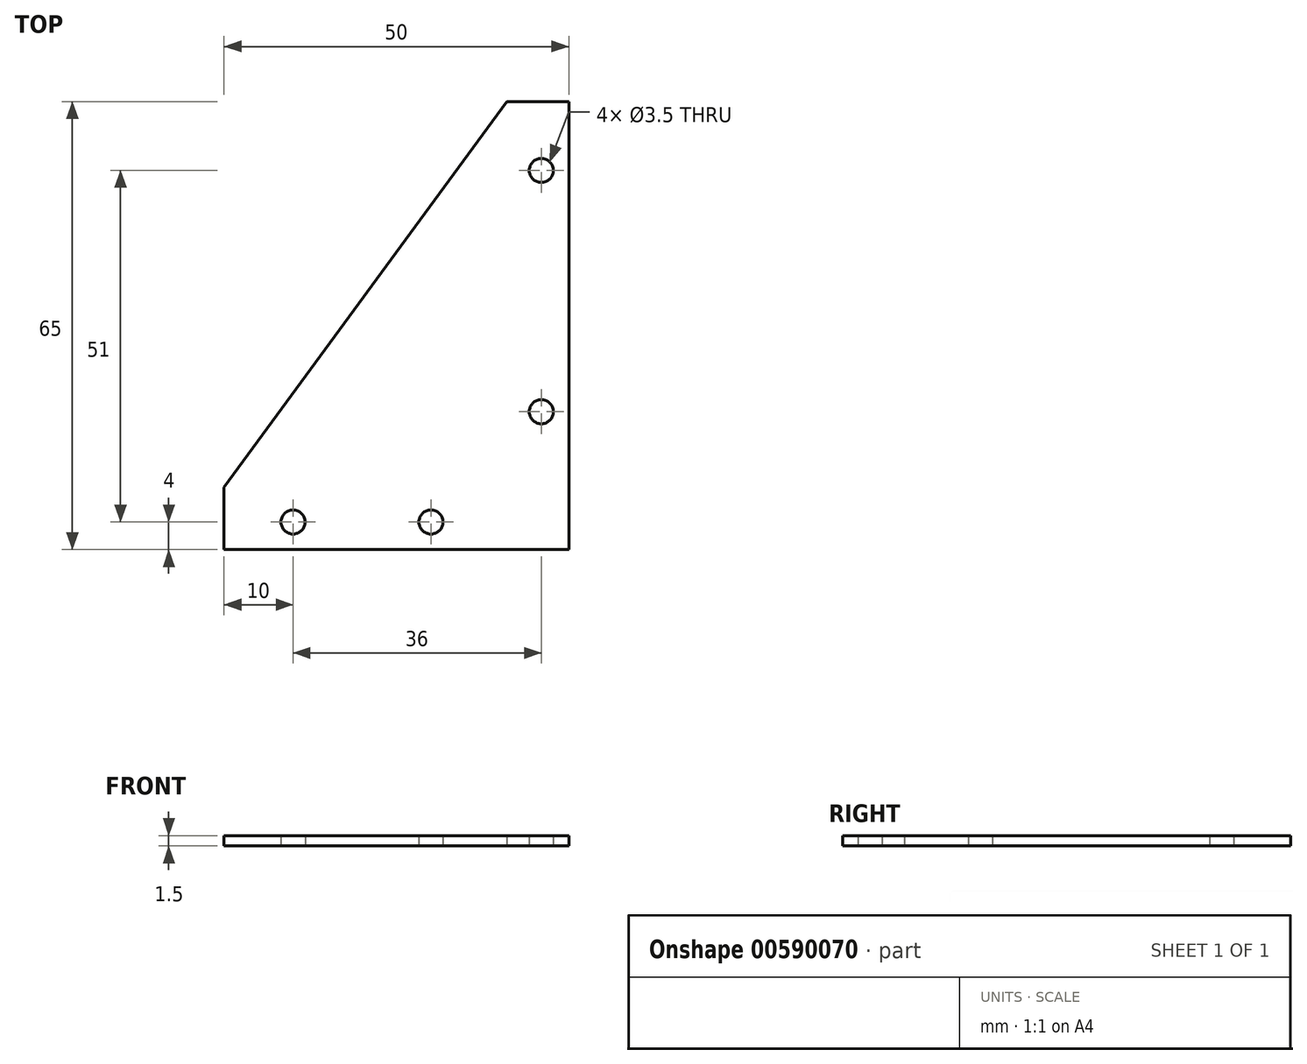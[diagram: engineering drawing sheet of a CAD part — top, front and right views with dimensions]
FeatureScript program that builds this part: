
annotation { "Feature Type Name" : "Feature", "Feature Type Description" : "" }
export const myFeature = defineFeature(function(context is Context, id is Id, definition is map)
    precondition{}
    {
        {
            var Q0;
            Q0=qCreatedBy(makeId("Top.planeOp"),FACE);
            var sketch = newSketch(context, id + "F0", { "sketchPlane" : qUnion([Q0])});
            skLineSegment(sketch, "E0.bottom", {"start": v(0, 0) * mm, "end": v(-50, 0) * mm});
            skLineSegment(sketch, "E0.top", {"start": v(0, 65) * mm, "end": v(-50, 65) * mm});
            skLineSegment(sketch, "E0.left", {"start": v(0, 0) * mm, "end": v(0, 65) * mm});
            skLineSegment(sketch, "E0.right", {"start": v(-50, 0) * mm, "end": v(-50, 65) * mm});
            skLineSegment(sketch, "E1", {"start": v(-9, 65) * mm, "end": v(-50, 9) * mm});
            skCircle(sketch, "E2", {"center": v(-4, 55) * mm, "radius": 1.75 * mm});
            skCircle(sketch, "E3", {"center": v(-40, 4) * mm, "radius": 1.75 * mm});
            skCircle(sketch, "E4", {"center": v(-20, 4) * mm, "radius": 1.75 * mm});
            skCircle(sketch, "E5", {"center": v(-4, 20) * mm, "radius": 1.75 * mm});
            skSolve(sketch);
        }
        {
            var Q0;
            {var subQ1=sQuery(id+"F0.wireOp",EDGE,"E0.bottom");Q0=makeQuery(id+"F0.imprint","IMPRINT",FACE,{"disambiguationData":[TD([[makeQuery(id+"F0.imprint","IMPRINT",EDGE,{"derivedFrom":subQ1}),-1.0]])]});}
            extrude(context, id + "F1", {"entities" : qUnion([Q0]), "depth" : 1.5 * mm, "offsetDistance" : 25 * mm});
        }
    });
